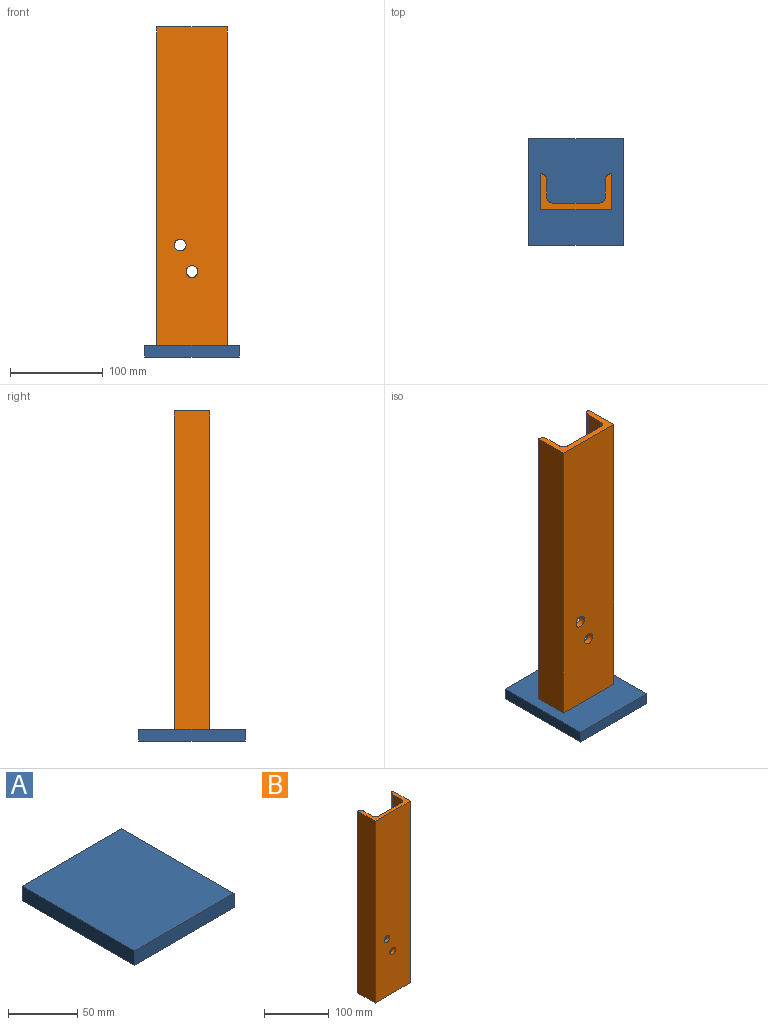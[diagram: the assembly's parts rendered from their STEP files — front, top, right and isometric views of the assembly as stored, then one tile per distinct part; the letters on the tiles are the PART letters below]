
ASSEMBLY  parts=2 mates=1
PART A: 6 faces, bbox 101.6x114.3x12.7 mm
  f0: plane 101.6x12.7mm, normal (0,1,0), area 1290.3mm2, adj f1,f3,f4,f5
  f1: plane 114.3x12.7mm, normal (-1,0,0), area 1451.6mm2, adj f0,f2,f4,f5
  f2: plane 101.6x12.7mm, normal (0,-1,0), area 1290.3mm2, adj f1,f3,f4,f5
  f3: plane 114.3x12.7mm, normal (1,0,0), area 1451.6mm2, adj f0,f2,f4,f5
  f4: plane 114.3x101.6mm, normal (0,0,1), area 11612.9mm2, adj f0,f1,f2,f3
  f5: plane 114.3x101.6mm, normal (0,0,-1), area 11612.9mm2, adj f0,f1,f2,f3
PART B: 16 faces, bbox 76.2x38.1x342.9 mm
  f0: plane 342.9x38.1mm, normal (-1,0,0), area 13064.5mm2, adj f1,f11,f12,f13
  f1: plane 342.9x76.2mm, normal (0,-1,0), area 25875.6mm2, adj f0,f2,f12,f13,f14,f15
  f2: plane 342.9x38.1mm, normal (1,0,0), area 13064.5mm2, adj f1,f3,f12,f13
  f3: plane 342.9x0.2mm, normal (0,1,0), area 69.7mm2, adj f2,f4,f12,f13
  f4: cylinder r=6.35mm len=342.9mm, axis (0,0,-1), area 3420.3mm2, adj f3,f5,f12,f13
  f5: plane 342.9x18.85mm, normal (-1,0,0), area 6462.6mm2, adj f4,f6,f12,f13
  f6: cylinder r=6.35mm len=342.9mm, axis (0,0,-1), area 3420.3mm2, adj f5,f7,f12,f13
  f7: plane 342.9x50.39mm, normal (0,1,0), area 17026.6mm2, adj f6,f8,f12,f13,f14,f15
  f8: cylinder r=6.35mm len=342.9mm, axis (0,0,-1), area 3420.3mm2, adj f7,f9,f12,f13
  f9: plane 342.9x18.85mm, normal (1,0,0), area 6462.6mm2, adj f8,f10,f12,f13
  f10: cylinder r=6.35mm len=342.9mm, axis (0,0,-1), area 3420.3mm2, adj f9,f11,f12,f13
  f11: plane 342.9x0.2mm, normal (0,1,0), area 69.7mm2, adj f0,f10,f12,f13
  f12: plane 76.2x38.1mm, normal (0,0,1), area 912.8mm2, adj f0,f1,f2,f3,f4,f5,f6,f7
  f13: plane 76.2x38.1mm, normal (0,0,-1), area 912.8mm2, adj f0,f1,f2,f3,f4,f5,f6,f7
  f14: cylinder r=6.35mm len=12.7mm, axis (0,-1,0), area 261.5mm2, adj f1,f7
  f15: cylinder r=6.35mm len=12.7mm, axis (0,-1,0), area 261.5mm2, adj f1,f7
PLACE A t=(-130.35,15.12,55.11)mm
PLACE B t=(-254.8,18.26,67.81)mm
MATE fastened A.f4 <-> B.f13  axis (0,0,1) through (-201.98,-5.23,67.81)mm
